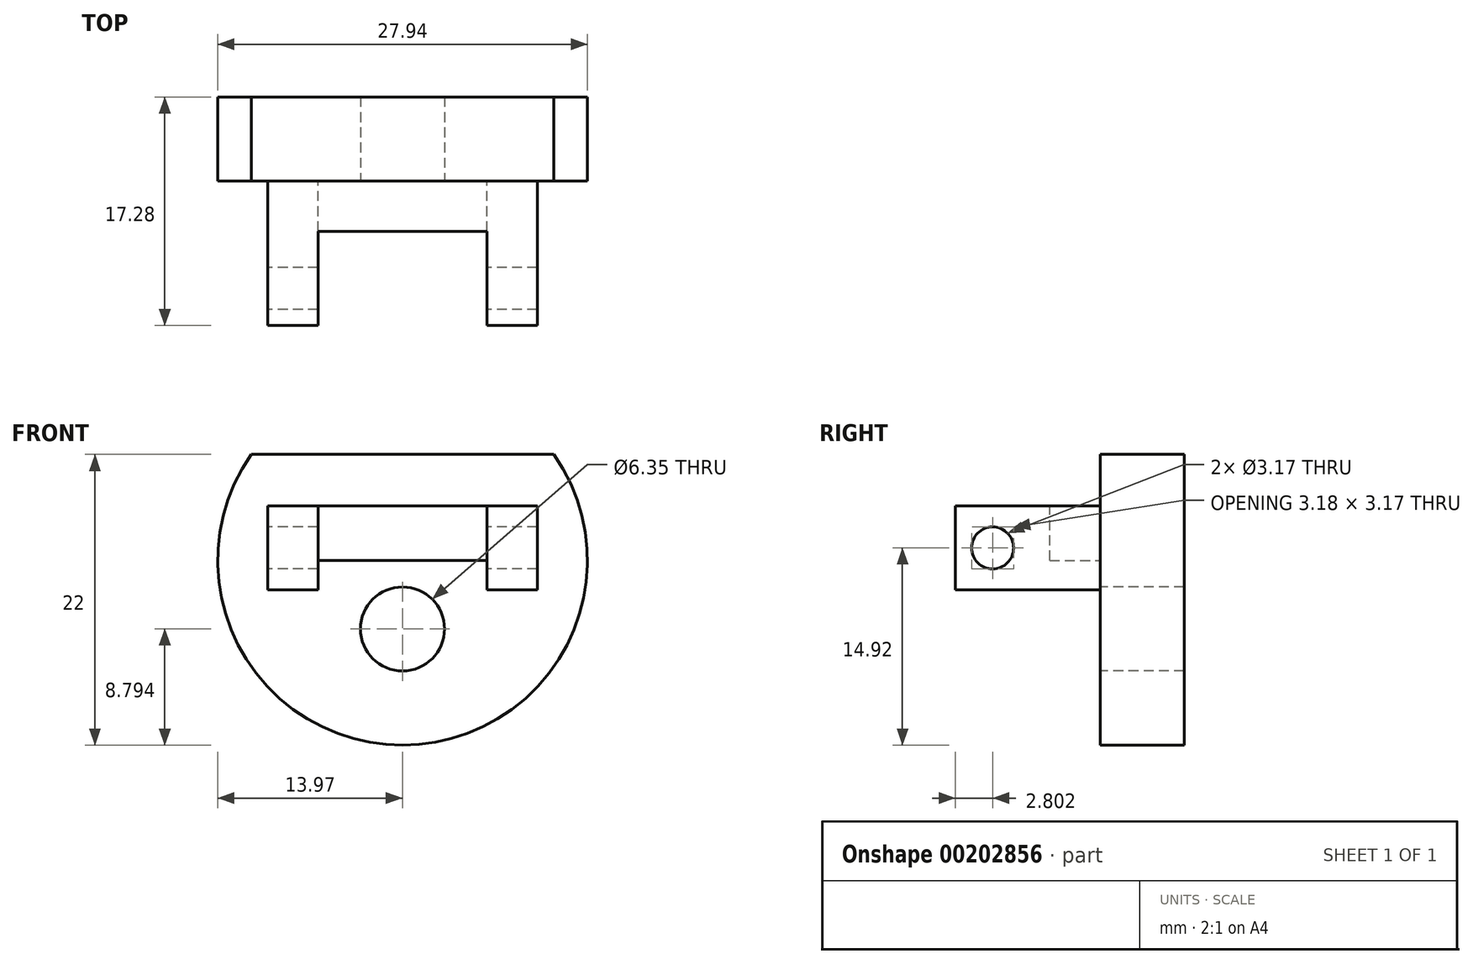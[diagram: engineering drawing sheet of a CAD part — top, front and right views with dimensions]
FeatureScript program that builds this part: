
annotation { "Feature Type Name" : "Feature", "Feature Type Description" : "" }
export const myFeature = defineFeature(function(context is Context, id is Id, definition is map)
    precondition{}
    {
        {
            var Q0;
            Q0=qCreatedBy(makeId("Front.planeOp"),FACE);
            var sketch = newSketch(context, id + "F0", { "sketchPlane" : qUnion([Q0])});
            skArc(sketch, "E0", {"start": v(-11.43, 8.03) * mm, "mid": v(0, -13.97) * mm, "end": v(11.43, 8.03) * mm});
            skLineSegment(sketch, "E1", {"start": v(-11.43, 8.03) * mm, "end": v(11.43, 8.03) * mm});
            skSolve(sketch);
        }
        {
            var Q0;
            Q0 = qSketchRegion(id + "F0", true);
            extrude(context, id + "F1", {"entities" : qUnion([Q0]), "depth" : 6.35 * mm});
        }
        {
            var Q0;
            Q0=makeQuery(id+"F1.opExtrude","CAP_FACE",FACE,{"disambiguationData":[OSD([sQuery(id+"F0.wireOp",EDGE,"E0"),sQuery(id+"F0.wireOp",EDGE,"E1")])],"isStart":false});
            var sketch = newSketch(context, id + "F2", { "sketchPlane" : qUnion([Q0])});
            skLineSegment(sketch, "E2", {"start": v(0, 8.03) * mm, "end": v(0, -5.18) * mm});
            skLineSegment(sketch, "E3", {"start": v(-10.19, 8.03) * mm, "end": v(-10.19, 4.13) * mm});
            skLineSegment(sketch, "E4", {"start": v(10.19, 8.03) * mm, "end": v(10.19, 4.13) * mm});
            skLineSegment(sketch, "E5", {"start": v(-10.19, 8.03) * mm, "end": v(10.19, 8.03) * mm});
            skLineSegment(sketch, "E6", {"start": v(10.19, 4.13) * mm, "end": v(10.19, -2.22) * mm});
            skPoint(sketch, "E7.middle", {"position": v(10.19, 0.95) * mm});
            skLineSegment(sketch, "E8.left", {"start": v(-10.19, 4.13) * mm, "end": v(-10.19, -2.22) * mm});
            skLineSegment(sketch, "E9", {"start": v(-10.19, 4.13) * mm, "end": v(-6.38, 4.13) * mm});
            skLineSegment(sketch, "E10", {"start": v(-6.38, 4.13) * mm, "end": v(-6.38, -2.22) * mm});
            skLineSegment(sketch, "E11", {"start": v(-6.38, -2.22) * mm, "end": v(-10.19, -2.22) * mm});
            skLineSegment(sketch, "E12", {"start": v(10.19, -2.22) * mm, "end": v(6.38, -2.22) * mm});
            skLineSegment(sketch, "E13", {"start": v(6.38, -2.22) * mm, "end": v(6.38, 4.13) * mm});
            skLineSegment(sketch, "E14", {"start": v(6.38, 4.13) * mm, "end": v(10.19, 4.13) * mm});
            skSolve(sketch);
        }
        {
            var Q0;
            Q0=sQuery(id+"F2.wireOp",VERTEX,"E2.end");
            var Q1;
            Q1=makeQuery(id+"F1.opExtrude","SWEPT_BODY",BODY,{"disambiguationData":[OSD([sQuery(id+"F0.wireOp",EDGE,"E0"),sQuery(id+"F0.wireOp",EDGE,"E1")])]});
            hole(context, id + "F3", {"style" : HoleStyle.SIMPLE, "endStyle" : HoleEndStyle.THROUGH, "holeDiameter" : 6.35 * mm, "locations" : qUnion([Q0]), "scope" : qUnion([Q1]), "isTappedThrough" : true});
        }
        {
            var Q0;
            Q0 = qSketchRegion(id + "F2", true);
            extrude(context, id + "F4", {"entities" : qUnion([Q0]), "operationType" : NewBodyOperationType.ADD, "depth" : 10.93 * mm});
        }
        {
            var Q0;
            {var subQ0=sQuery(id+"F2.wireOp",EDGE,"E8.left");Q0=makeQuery(id+"F4.boolean.opBoolean","MERGE",FACE,{"derivedFrom":[makeQuery(id+"FSZYfVx7t9bt6gJ_1.opExtrude","SWEPT_FACE",FACE,{"disambiguationData":[OSD([subQ0])]}),makeQuery(id+"F4.opExtrude","SWEPT_FACE",FACE,{"disambiguationData":[OSD([subQ0])]})]});}
            var sketch = newSketch(context, id + "F5", { "sketchPlane" : qUnion([Q0])});
            skLineSegment(sketch, "E15", {"start": v(6.35, 0.95) * mm, "end": v(14.48, 0.95) * mm});
            skCircle(sketch, "E16", {"center": v(14.48, 0.95) * mm, "radius": 1.59 * mm});
            skLineSegment(sketch, "E17", {"start": v(14.48, 0.95) * mm, "end": v(17.28, 4.13) * mm});
            skLineSegment(sketch, "E18", {"start": v(17.28, 4.13) * mm, "end": v(15.53, 2.14) * mm});
            skSolve(sketch);
        }
        {
            var Q0;
            Q0=sQuery(id+"F5.wireOp",VERTEX,"06yTfRHD-bwlF-H4mc-tL8S-cTHUh1dLqGAm.end");
            var Q1;
            Q1=sQuery(id+"F5.wireOp",VERTEX,"E15.end");
            var Q2;
            Q2=makeQuery(id+"F1.opExtrude","SWEPT_BODY",BODY,{"disambiguationData":[OSD([sQuery(id+"F0.wireOp",EDGE,"E0"),sQuery(id+"F0.wireOp",EDGE,"E1")])]});
            hole(context, id + "F6", {"style" : HoleStyle.SIMPLE, "endStyle" : HoleEndStyle.THROUGH, "holeDiameter" : 3.17 * mm, "locations" : qUnion([Q0, Q1]), "scope" : qUnion([Q2]), "isTappedThrough" : true});
        }
        {
            var Q0;
            Q0=makeQuery(id+"F1.opExtrude","CAP_FACE",FACE,{"disambiguationData":[OSD([sQuery(id+"F0.wireOp",EDGE,"E0"),sQuery(id+"F0.wireOp",EDGE,"E1")])],"isStart":false});
            var sketch = newSketch(context, id + "F7", { "sketchPlane" : qUnion([Q0])});
            skLineSegment(sketch, "E19.bottom", {"start": v(-6.38, 4.13) * mm, "end": v(6.38, 4.13) * mm});
            skLineSegment(sketch, "E19.top", {"start": v(-6.38, 0) * mm, "end": v(6.38, 0) * mm});
            skLineSegment(sketch, "E19.left", {"start": v(-6.38, 4.13) * mm, "end": v(-6.38, 0) * mm});
            skLineSegment(sketch, "E19.right", {"start": v(6.38, 4.13) * mm, "end": v(6.38, 0) * mm});
            skSolve(sketch);
        }
        {
            var Q0;
            Q0 = qSketchRegion(id + "F7", true);
            extrude(context, id + "F8", {"entities" : qUnion([Q0]), "operationType" : NewBodyOperationType.ADD, "depth" : 3.8 * mm});
        }
    });
